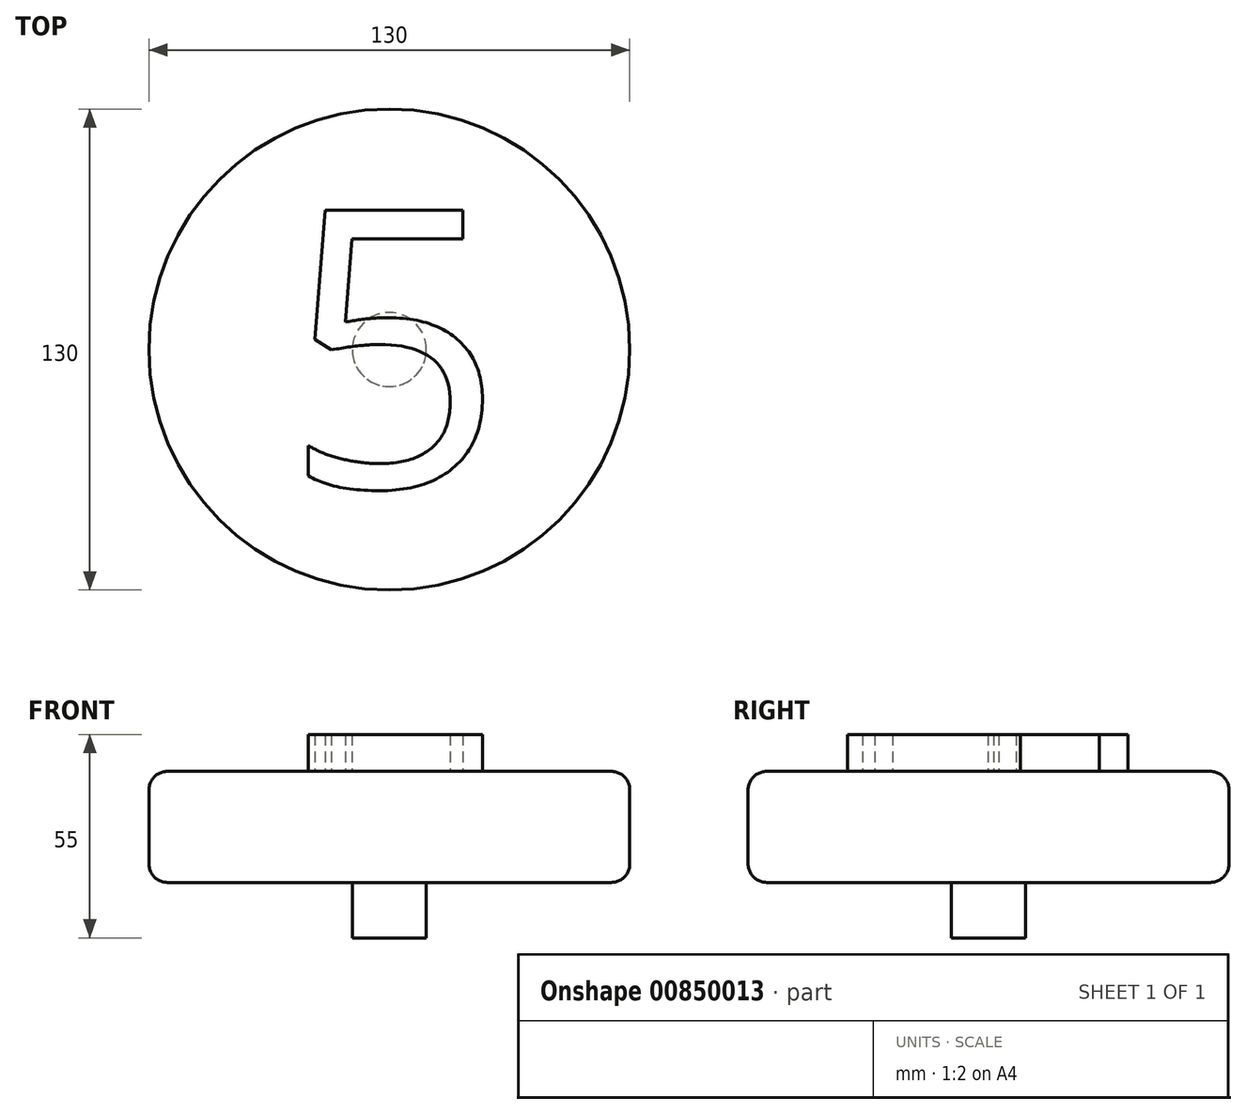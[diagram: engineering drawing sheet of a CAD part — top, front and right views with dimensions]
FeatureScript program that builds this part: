
annotation { "Feature Type Name" : "Feature", "Feature Type Description" : "" }
export const myFeature = defineFeature(function(context is Context, id is Id, definition is map)
    precondition{}
    {
        {
            var Q0;
            Q0=qCreatedBy(makeId("Top.planeOp"),FACE);
            var sketch = newSketch(context, id + "F0", { "sketchPlane" : qUnion([Q0])});
            skCircle(sketch, "E0", {"center": v(0, 0) * mm, "radius": 65 * mm});
            skSolve(sketch);
        }
        {
            var Q0;
            Q0=makeQuery(id+"F0.imprint","IMPRINT",FACE,{"disambiguationData":[TD([[makeQuery(id+"F0.imprint","IMPRINT",EDGE,{"derivedFrom":sQuery(id+"F0.wireOp",EDGE,"E0")}),1.0]])]});
            extrude(context, id + "F1", {"entities" : qUnion([Q0]), "depth" : 30 * mm, "offsetDistance" : 25 * mm});
        }
        {
            var Q0;
            Q0=makeQuery(id+"F1.opExtrude","CAP_FACE",FACE,{"disambiguationData":[OSD([sQuery(id+"F0.wireOp",EDGE,"E0")])],"isStart":false});
            var sketch = newSketch(context, id + "F2", { "sketchPlane" : qUnion([Q0])});
            skText(sketch, "E1", { "text": "5", "fontName": "OpenSans-Regular.ttf"});
            const initialGuessF2  = {"E1": [-0.02874, -0.0371, 1, 0, 0.07547]};
            skSetInitialGuess(sketch, initialGuessF2);
            skSolve(sketch);
        }
        {
            var Q0;
            Q0=makeQuery(id+"F2.imprint","IMPRINT",FACE,{"disambiguationData":[TD([[makeQuery(id+"F2.imprint","IMPRINT",EDGE,{"derivedFrom":sQuery(id+"F2.wireOp",EDGE,"E1.sketch_text.stroke-0")}),-1.0]])]});
            extrude(context, id + "F3", {"entities" : qUnion([Q0]), "operationType" : NewBodyOperationType.ADD, "depth" : 10 * mm, "offsetDistance" : 25 * mm});
        }
        {
            var Q0;
            Q0=makeQuery(id+"F1.opExtrude","CAP_EDGE",EDGE,{"disambiguationData":[OSD([sQuery(id+"F0.wireOp",EDGE,"E0")])],"isStart":false});
            var Q1;
            Q1=makeQuery(id+"F1.opExtrude","SWEPT_FACE",FACE,{"disambiguationData":[OSD([sQuery(id+"F0.wireOp",EDGE,"E0")])]});
            fillet(context, id + "F4", {"entities" : qUnion([Q0, Q1]), "radius" : 5 * mm, "tangentPropagation" : true, "allowEdgeOverflow" : false});
        }
        {
            var Q0;
            Q0=makeQuery(id+"F1.opExtrude","CAP_FACE",FACE,{"disambiguationData":[OSD([sQuery(id+"F0.wireOp",EDGE,"E0")])],"isStart":true});
            var sketch = newSketch(context, id + "F5", { "sketchPlane" : qUnion([Q0])});
            skCircle(sketch, "E2", {"center": v(0, 0) * mm, "radius": 10 * mm});
            skSolve(sketch);
        }
        {
            var Q0;
            Q0=makeQuery(id+"F5.imprint","IMPRINT",FACE,{"disambiguationData":[TD([[makeQuery(id+"F5.imprint","IMPRINT",EDGE,{"derivedFrom":sQuery(id+"F5.wireOp",EDGE,"E2")}),1.0]])]});
            extrude(context, id + "F6", {"entities" : qUnion([Q0]), "operationType" : NewBodyOperationType.ADD, "depth" : 15 * mm, "offsetDistance" : 25 * mm});
        }
    });
